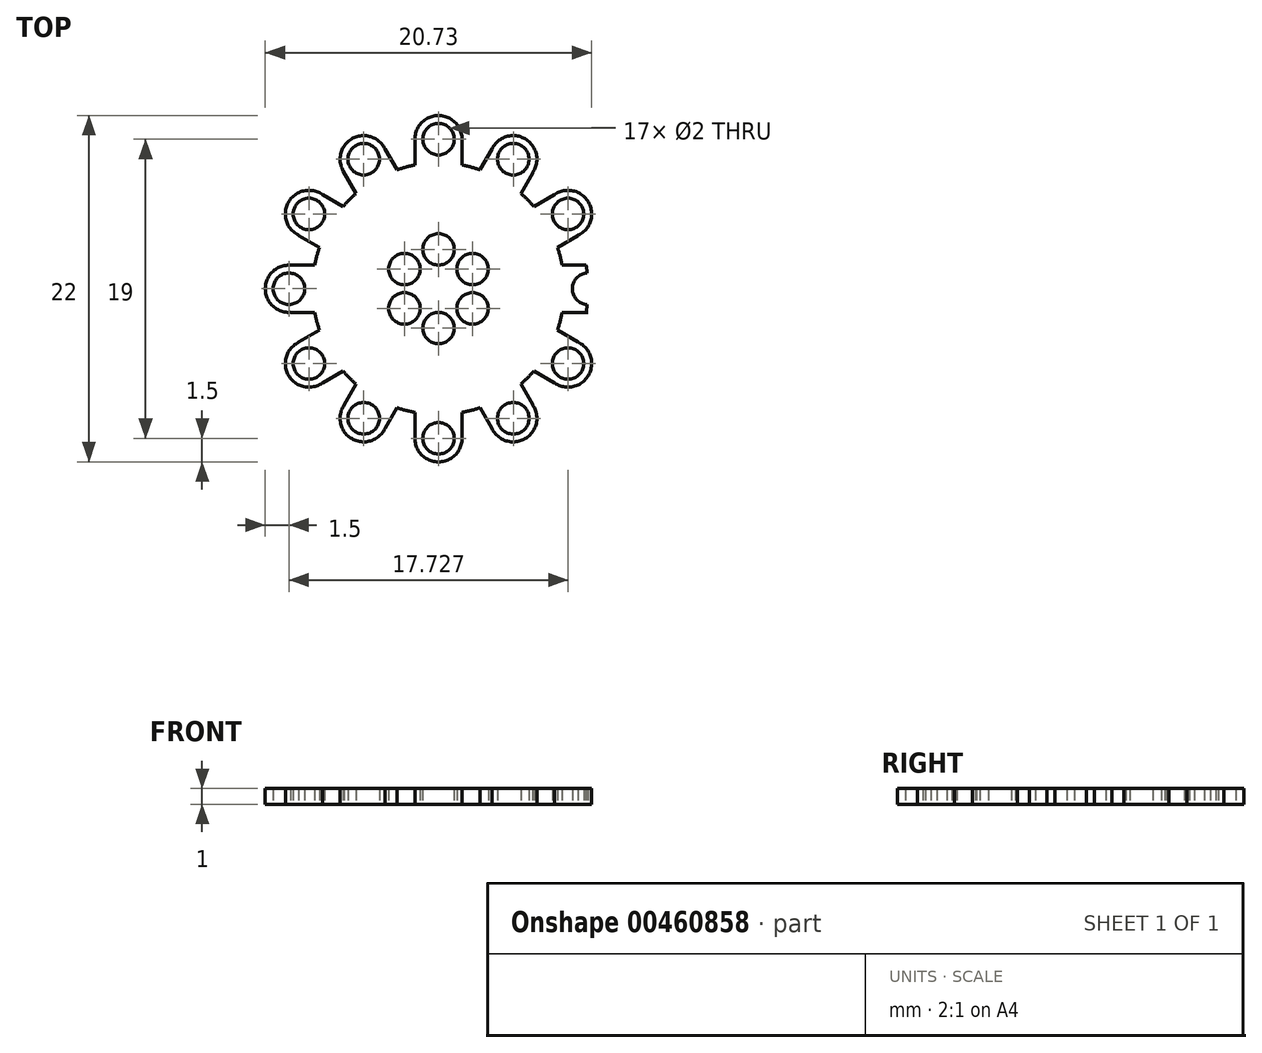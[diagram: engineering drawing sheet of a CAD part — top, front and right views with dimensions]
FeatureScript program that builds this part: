
annotation { "Feature Type Name" : "Feature", "Feature Type Description" : "" }
export const myFeature = defineFeature(function(context is Context, id is Id, definition is map)
    precondition{}
    {
        {
            var Q0;
            Q0=qCreatedBy(makeId("Top.planeOp"),FACE);
            var sketch = newSketch(context, id + "F0", { "sketchPlane" : qUnion([Q0])});
            skCircle(sketch, "E0", {"center": v(0, 0) * mm, "radius": 9.5 * mm});
            skCircle(sketch, "E1", {"center": v(0, 0) * mm, "radius": 2.5 * mm});
            skCircle(sketch, "E2", {"center": v(0, 2.5) * mm, "radius": 1 * mm});
            skCircle(sketch, "E3.1.0", {"center": v(-2.17, 1.25) * mm, "radius": 1 * mm});
            skCircle(sketch, "E3.2.0", {"center": v(-2.17, -1.25) * mm, "radius": 1 * mm});
            skCircle(sketch, "E3.3.0", {"center": v(0, -2.5) * mm, "radius": 1 * mm});
            skCircle(sketch, "E3.4.0", {"center": v(2.17, -1.25) * mm, "radius": 1 * mm});
            skCircle(sketch, "E3.5.0", {"center": v(2.17, 1.25) * mm, "radius": 1 * mm});
            skCircle(sketch, "E4", {"center": v(0, 0) * mm, "radius": 8 * mm});
            skLineSegment(sketch, "E5.anchor1", {"start": v(0, 0) * mm, "end": v(0, 8) * mm, "construction": true});
            skLineSegment(sketch, "E5.anchor2", {"start": v(0, 0) * mm, "end": v(-4, 6.93) * mm, "construction": true});
            skCircle(sketch, "E6", {"center": v(0, 9.5) * mm, "radius": 1 * mm});
            skCircle(sketch, "E7.1.0", {"center": v(-4.75, 8.23) * mm, "radius": 1 * mm});
            skCircle(sketch, "E7.2.0", {"center": v(-8.23, 4.75) * mm, "radius": 1 * mm});
            skCircle(sketch, "E7.3.0", {"center": v(-9.5, 0) * mm, "radius": 1 * mm});
            skCircle(sketch, "E7.4.0", {"center": v(-8.23, -4.75) * mm, "radius": 1 * mm});
            skCircle(sketch, "E7.5.0", {"center": v(-4.75, -8.23) * mm, "radius": 1 * mm});
            skCircle(sketch, "E7.6.0", {"center": v(0, -9.5) * mm, "radius": 1 * mm});
            skCircle(sketch, "E7.7.0", {"center": v(4.75, -8.23) * mm, "radius": 1 * mm});
            skCircle(sketch, "E7.8.0", {"center": v(8.23, -4.75) * mm, "radius": 1 * mm});
            skCircle(sketch, "E7.9.0", {"center": v(9.5, 0) * mm, "radius": 1 * mm});
            skCircle(sketch, "E7.10.0", {"center": v(8.23, 4.75) * mm, "radius": 1 * mm});
            skCircle(sketch, "E7.11.0", {"center": v(4.75, 8.23) * mm, "radius": 1 * mm});
            skArc(sketch, "E8", {"start": v(1.5, 9.38) * mm, "mid": v(0, 11) * mm, "end": v(-1.5, 9.38) * mm});
            skArc(sketch, "E9.1.0", {"start": v(-3.4, 8.87) * mm, "mid": v(-5.45, 9.55) * mm, "end": v(-6.05, 7.48) * mm});
            skArc(sketch, "E9.2.0", {"start": v(-7.38, 5.99) * mm, "mid": v(-9.53, 5.5) * mm, "end": v(-8.87, 3.4) * mm});
            skArc(sketch, "E9.3.0", {"start": v(-9.38, 1.5) * mm, "mid": v(-11, 0) * mm, "end": v(-9.38, -1.5) * mm});
            skArc(sketch, "E9.4.0", {"start": v(-8.87, -3.4) * mm, "mid": v(-9.53, -5.5) * mm, "end": v(-7.38, -5.99) * mm});
            skArc(sketch, "E9.5.0", {"start": v(-5.99, -7.38) * mm, "mid": v(-5.5, -9.53) * mm, "end": v(-3.4, -8.87) * mm});
            skArc(sketch, "E9.6.0", {"start": v(-1.5, -9.38) * mm, "mid": v(0, -11) * mm, "end": v(1.5, -9.38) * mm});
            skArc(sketch, "E9.7.0", {"start": v(3.4, -8.87) * mm, "mid": v(5.5, -9.53) * mm, "end": v(5.99, -7.38) * mm});
            skArc(sketch, "E9.8.0", {"start": v(7.38, -5.99) * mm, "mid": v(9.53, -5.5) * mm, "end": v(8.87, -3.4) * mm});
            skArc(sketch, "E9.9.0", {"start": v(9.38, -1.5) * mm, "mid": v(11, 0) * mm, "end": v(9.38, 1.5) * mm});
            skArc(sketch, "E9.10.0", {"start": v(8.87, 3.4) * mm, "mid": v(9.53, 5.5) * mm, "end": v(7.38, 5.99) * mm});
            skArc(sketch, "E9.11.0", {"start": v(5.99, 7.38) * mm, "mid": v(5.5, 9.53) * mm, "end": v(3.4, 8.87) * mm});
            skLineSegment(sketch, "E10", {"start": v(-1.5, 9.5) * mm, "end": v(-1.5, 7.86) * mm});
            skLineSegment(sketch, "E11", {"start": v(1.5, 9.5) * mm, "end": v(1.5, 7.86) * mm});
            skArc(sketch, "E12.1.0", {"start": v(-8.87, -3.4) * mm, "mid": v(-9.55, -5.45) * mm, "end": v(-7.48, -6.05) * mm});
            skLineSegment(sketch, "E13.1.0", {"start": v(-3.45, 8.98) * mm, "end": v(-2.63, 7.56) * mm});
            skLineSegment(sketch, "E13.2.0", {"start": v(-7.48, 6.05) * mm, "end": v(-6.06, 5.23) * mm});
            skLineSegment(sketch, "E13.3.0", {"start": v(-9.5, 1.5) * mm, "end": v(-7.86, 1.5) * mm});
            skLineSegment(sketch, "E13.4.0", {"start": v(-8.98, -3.45) * mm, "end": v(-7.56, -2.63) * mm});
            skLineSegment(sketch, "E13.5.0", {"start": v(-6.05, -7.48) * mm, "end": v(-5.23, -6.06) * mm});
            skLineSegment(sketch, "E13.6.0", {"start": v(-1.5, -9.5) * mm, "end": v(-1.5, -7.86) * mm});
            skLineSegment(sketch, "E13.7.0", {"start": v(3.45, -8.98) * mm, "end": v(2.63, -7.56) * mm});
            skLineSegment(sketch, "E13.8.0", {"start": v(7.48, -6.05) * mm, "end": v(6.06, -5.23) * mm});
            skLineSegment(sketch, "E13.9.0", {"start": v(9.5, -1.5) * mm, "end": v(7.86, -1.5) * mm});
            skLineSegment(sketch, "E13.10.0", {"start": v(8.98, 3.45) * mm, "end": v(7.56, 2.63) * mm});
            skLineSegment(sketch, "E13.11.0", {"start": v(6.05, 7.48) * mm, "end": v(5.23, 6.06) * mm});
            skLineSegment(sketch, "E14.1.0", {"start": v(-6.05, 7.48) * mm, "end": v(-5.23, 6.06) * mm});
            skLineSegment(sketch, "E14.2.0", {"start": v(-8.98, 3.45) * mm, "end": v(-7.56, 2.63) * mm});
            skLineSegment(sketch, "E14.3.0", {"start": v(-9.5, -1.5) * mm, "end": v(-7.86, -1.5) * mm});
            skLineSegment(sketch, "E14.4.0", {"start": v(-7.48, -6.05) * mm, "end": v(-6.06, -5.23) * mm});
            skLineSegment(sketch, "E14.5.0", {"start": v(-3.45, -8.98) * mm, "end": v(-2.63, -7.56) * mm});
            skLineSegment(sketch, "E14.6.0", {"start": v(1.5, -9.5) * mm, "end": v(1.5, -7.86) * mm});
            skLineSegment(sketch, "E14.7.0", {"start": v(6.05, -7.48) * mm, "end": v(5.23, -6.06) * mm});
            skLineSegment(sketch, "E14.8.0", {"start": v(8.98, -3.45) * mm, "end": v(7.56, -2.63) * mm});
            skLineSegment(sketch, "E14.9.0", {"start": v(9.5, 1.5) * mm, "end": v(7.86, 1.5) * mm});
            skLineSegment(sketch, "E14.10.0", {"start": v(7.48, 6.05) * mm, "end": v(6.06, 5.23) * mm});
            skLineSegment(sketch, "E14.11.0", {"start": v(3.45, 8.98) * mm, "end": v(2.63, 7.56) * mm});
            skSolve(sketch);
        }
        {
            var Q0;
            {var subQ11=sQuery(id+"F0.wireOp",EDGE,"E3.5.0");var subQ12=sQuery(id+"F0.wireOp",EDGE,"E1");var subQ13=makeQuery(id+"F0.imprint","INTERSECT",VERTEX,{"disambiguationData":[OD(0.0)],"derivedFrom":[subQ12,subQ11]});Q0=makeQuery(id+"F0.imprint","IMPRINT",FACE,{"disambiguationData":[TD([[makeQuery(id+"F0.imprint","IMPRINT",EDGE,{"disambiguationData":[TD([[subQ13,-1.0]])],"derivedFrom":subQ12}),-1.0]])]});}
            var Q1;
            {var subQ0=sQuery(id+"F0.wireOp",EDGE,"E9.8.0");var subQ1=sQuery(id+"F0.wireOp",EDGE,"E0");var subQ12=makeQuery(id+"F0.imprint","INTERSECT",VERTEX,{"disambiguationData":[OD(0.0)],"derivedFrom":[subQ1,subQ0]});Q1=makeQuery(id+"F0.imprint","IMPRINT",FACE,{"disambiguationData":[TD([[makeQuery(id+"F0.imprint","IMPRINT",EDGE,{"disambiguationData":[TD([[subQ12,1.0]])],"derivedFrom":subQ1}),1.0]])]});}
            var Q2;
            {var subQ0=sQuery(id+"F0.wireOp",EDGE,"E9.8.0");var subQ1=sQuery(id+"F0.wireOp",EDGE,"E0");var subQ2=makeQuery(id+"F0.imprint","INTERSECT",VERTEX,{"disambiguationData":[OD(0.0)],"derivedFrom":[subQ1,subQ0]});Q2=makeQuery(id+"F0.imprint","IMPRINT",FACE,{"disambiguationData":[TD([[makeQuery(id+"F0.imprint","IMPRINT",EDGE,{"disambiguationData":[TD([[subQ2,-1.0]])],"derivedFrom":subQ1}),-1.0]])]});}
            var Q3;
            {var subQ0=sQuery(id+"F0.wireOp",EDGE,"E9.9.0");var subQ1=sQuery(id+"F0.wireOp",EDGE,"E0");var subQ7=makeQuery(id+"F0.imprint","INTERSECT",VERTEX,{"disambiguationData":[OD(1.0)],"derivedFrom":[subQ1,subQ0]});Q3=makeQuery(id+"F0.imprint","IMPRINT",FACE,{"disambiguationData":[TD([[makeQuery(id+"F0.imprint","IMPRINT",EDGE,{"disambiguationData":[TD([[subQ7,1.0]])],"derivedFrom":subQ1}),1.0]])]});}
            var Q4;
            {var subQ0=sQuery(id+"F0.wireOp",EDGE,"E9.9.0");var subQ1=sQuery(id+"F0.wireOp",EDGE,"E0");var subQ7=makeQuery(id+"F0.imprint","INTERSECT",VERTEX,{"disambiguationData":[OD(1.0)],"derivedFrom":[subQ1,subQ0]});Q4=makeQuery(id+"F0.imprint","IMPRINT",FACE,{"disambiguationData":[TD([[makeQuery(id+"F0.imprint","IMPRINT",EDGE,{"disambiguationData":[TD([[subQ7,1.0]])],"derivedFrom":subQ1}),-1.0]])]});}
            var Q5;
            {var subQ0=sQuery(id+"F0.wireOp",EDGE,"E9.10.0");var subQ1=sQuery(id+"F0.wireOp",EDGE,"E0");var subQ8=makeQuery(id+"F0.imprint","INTERSECT",VERTEX,{"disambiguationData":[OD(0.0)],"derivedFrom":[subQ1,subQ0]});Q5=makeQuery(id+"F0.imprint","IMPRINT",FACE,{"disambiguationData":[TD([[makeQuery(id+"F0.imprint","IMPRINT",EDGE,{"disambiguationData":[TD([[subQ8,1.0]])],"derivedFrom":subQ1}),1.0]])]});}
            var Q6;
            {var subQ1=sQuery(id+"F0.wireOp",EDGE,"E0");var subQ4=sQuery(id+"F0.wireOp",EDGE,"E9.10.0");var subQ5=makeQuery(id+"F0.imprint","INTERSECT",VERTEX,{"disambiguationData":[OD(0.0)],"derivedFrom":[subQ1,subQ4]});Q6=makeQuery(id+"F0.imprint","IMPRINT",FACE,{"disambiguationData":[TD([[makeQuery(id+"F0.imprint","IMPRINT",EDGE,{"disambiguationData":[TD([[subQ5,-1.0]])],"derivedFrom":subQ1}),-1.0]])]});}
            var Q7;
            {var subQ0=sQuery(id+"F0.wireOp",EDGE,"E9.11.0");var subQ1=sQuery(id+"F0.wireOp",EDGE,"E0");var subQ7=makeQuery(id+"F0.imprint","INTERSECT",VERTEX,{"disambiguationData":[OD(0.0)],"derivedFrom":[subQ1,subQ0]});Q7=makeQuery(id+"F0.imprint","IMPRINT",FACE,{"disambiguationData":[TD([[makeQuery(id+"F0.imprint","IMPRINT",EDGE,{"disambiguationData":[TD([[subQ7,1.0]])],"derivedFrom":subQ1}),1.0]])]});}
            var Q8;
            {var subQ0=sQuery(id+"F0.wireOp",EDGE,"E9.11.0");var subQ1=sQuery(id+"F0.wireOp",EDGE,"E0");var subQ2=makeQuery(id+"F0.imprint","INTERSECT",VERTEX,{"disambiguationData":[OD(0.0)],"derivedFrom":[subQ1,subQ0]});Q8=makeQuery(id+"F0.imprint","IMPRINT",FACE,{"disambiguationData":[TD([[makeQuery(id+"F0.imprint","IMPRINT",EDGE,{"disambiguationData":[TD([[subQ2,-1.0]])],"derivedFrom":subQ1}),-1.0]])]});}
            var Q9;
            {var subQ0=sQuery(id+"F0.wireOp",EDGE,"E8");var subQ1=sQuery(id+"F0.wireOp",EDGE,"E0");var subQ9=makeQuery(id+"F0.imprint","INTERSECT",VERTEX,{"disambiguationData":[OD(0.0)],"derivedFrom":[subQ1,subQ0]});Q9=makeQuery(id+"F0.imprint","IMPRINT",FACE,{"disambiguationData":[TD([[makeQuery(id+"F0.imprint","IMPRINT",EDGE,{"disambiguationData":[TD([[subQ9,1.0]])],"derivedFrom":subQ1}),1.0]])]});}
            var Q10;
            {var subQ1=sQuery(id+"F0.wireOp",EDGE,"E0");var subQ4=sQuery(id+"F0.wireOp",EDGE,"E8");var subQ5=makeQuery(id+"F0.imprint","INTERSECT",VERTEX,{"disambiguationData":[OD(0.0)],"derivedFrom":[subQ1,subQ4]});Q10=makeQuery(id+"F0.imprint","IMPRINT",FACE,{"disambiguationData":[TD([[makeQuery(id+"F0.imprint","IMPRINT",EDGE,{"disambiguationData":[TD([[subQ5,-1.0]])],"derivedFrom":subQ1}),-1.0]])]});}
            var Q11;
            {var subQ1=sQuery(id+"F0.wireOp",EDGE,"E0");var subQ9=makeQuery(id+"F0.imprint","INTERSECT",VERTEX,{"derivedFrom":[subQ1,sQuery(id+"F0.wireOp",EDGE,"E9.1.0")]});Q11=makeQuery(id+"F0.imprint","IMPRINT",FACE,{"disambiguationData":[TD([[makeQuery(id+"F0.imprint","IMPRINT",EDGE,{"disambiguationData":[TD([[subQ9,1.0]])],"derivedFrom":subQ1}),1.0]])]});}
            var Q12;
            {var subQ0=sQuery(id+"F0.wireOp",EDGE,"E9.1.0");var subQ1=sQuery(id+"F0.wireOp",EDGE,"E0");var subQ2=makeQuery(id+"F0.imprint","INTERSECT",VERTEX,{"derivedFrom":[subQ1,subQ0]});Q12=makeQuery(id+"F0.imprint","IMPRINT",FACE,{"disambiguationData":[TD([[makeQuery(id+"F0.imprint","IMPRINT",EDGE,{"disambiguationData":[TD([[subQ2,-1.0]])],"derivedFrom":subQ1}),-1.0]])]});}
            var Q13;
            {var subQ0=sQuery(id+"F0.wireOp",EDGE,"E9.2.0");var subQ1=sQuery(id+"F0.wireOp",EDGE,"E0");var subQ7=makeQuery(id+"F0.imprint","INTERSECT",VERTEX,{"disambiguationData":[OD(0.0)],"derivedFrom":[subQ1,subQ0]});Q13=makeQuery(id+"F0.imprint","IMPRINT",FACE,{"disambiguationData":[TD([[makeQuery(id+"F0.imprint","IMPRINT",EDGE,{"disambiguationData":[TD([[subQ7,1.0]])],"derivedFrom":subQ1}),1.0]])]});}
            var Q14;
            {var subQ0=sQuery(id+"F0.wireOp",EDGE,"E9.2.0");var subQ1=sQuery(id+"F0.wireOp",EDGE,"E0");var subQ2=makeQuery(id+"F0.imprint","INTERSECT",VERTEX,{"disambiguationData":[OD(0.0)],"derivedFrom":[subQ1,subQ0]});Q14=makeQuery(id+"F0.imprint","IMPRINT",FACE,{"disambiguationData":[TD([[makeQuery(id+"F0.imprint","IMPRINT",EDGE,{"disambiguationData":[TD([[subQ2,-1.0]])],"derivedFrom":subQ1}),-1.0]])]});}
            var Q15;
            {var subQ0=sQuery(id+"F0.wireOp",EDGE,"E9.3.0");var subQ1=sQuery(id+"F0.wireOp",EDGE,"E0");var subQ7=makeQuery(id+"F0.imprint","INTERSECT",VERTEX,{"disambiguationData":[OD(0.0)],"derivedFrom":[subQ1,subQ0]});Q15=makeQuery(id+"F0.imprint","IMPRINT",FACE,{"disambiguationData":[TD([[makeQuery(id+"F0.imprint","IMPRINT",EDGE,{"disambiguationData":[TD([[subQ7,1.0]])],"derivedFrom":subQ1}),1.0]])]});}
            var Q16;
            {var subQ0=sQuery(id+"F0.wireOp",EDGE,"E9.3.0");var subQ1=sQuery(id+"F0.wireOp",EDGE,"E0");var subQ2=makeQuery(id+"F0.imprint","INTERSECT",VERTEX,{"disambiguationData":[OD(0.0)],"derivedFrom":[subQ1,subQ0]});Q16=makeQuery(id+"F0.imprint","IMPRINT",FACE,{"disambiguationData":[TD([[makeQuery(id+"F0.imprint","IMPRINT",EDGE,{"disambiguationData":[TD([[subQ2,-1.0]])],"derivedFrom":subQ1}),-1.0]])]});}
            var Q17;
            {var subQ0=sQuery(id+"F0.wireOp",EDGE,"E9.4.0");var subQ1=sQuery(id+"F0.wireOp",EDGE,"E0");var subQ11=makeQuery(id+"F0.imprint","INTERSECT",VERTEX,{"disambiguationData":[OD(0.0)],"derivedFrom":[subQ1,subQ0]});Q17=makeQuery(id+"F0.imprint","IMPRINT",FACE,{"disambiguationData":[TD([[makeQuery(id+"F0.imprint","IMPRINT",EDGE,{"disambiguationData":[TD([[subQ11,1.0]])],"derivedFrom":subQ1}),1.0]])]});}
            var Q18;
            {var subQ1=sQuery(id+"F0.wireOp",EDGE,"E0");var subQ4=sQuery(id+"F0.wireOp",EDGE,"E9.4.0");var subQ5=makeQuery(id+"F0.imprint","INTERSECT",VERTEX,{"disambiguationData":[OD(0.0)],"derivedFrom":[subQ1,subQ4]});Q18=makeQuery(id+"F0.imprint","IMPRINT",FACE,{"disambiguationData":[TD([[makeQuery(id+"F0.imprint","IMPRINT",EDGE,{"disambiguationData":[TD([[subQ5,-1.0]])],"derivedFrom":subQ1}),-1.0]])]});}
            var Q19;
            {var subQ0=sQuery(id+"F0.wireOp",EDGE,"E9.5.0");var subQ1=sQuery(id+"F0.wireOp",EDGE,"E0");var subQ12=makeQuery(id+"F0.imprint","INTERSECT",VERTEX,{"disambiguationData":[OD(0.0)],"derivedFrom":[subQ1,subQ0]});Q19=makeQuery(id+"F0.imprint","IMPRINT",FACE,{"disambiguationData":[TD([[makeQuery(id+"F0.imprint","IMPRINT",EDGE,{"disambiguationData":[TD([[subQ12,1.0]])],"derivedFrom":subQ1}),1.0]])]});}
            var Q20;
            {var subQ0=sQuery(id+"F0.wireOp",EDGE,"E9.5.0");var subQ1=sQuery(id+"F0.wireOp",EDGE,"E0");var subQ2=makeQuery(id+"F0.imprint","INTERSECT",VERTEX,{"disambiguationData":[OD(0.0)],"derivedFrom":[subQ1,subQ0]});Q20=makeQuery(id+"F0.imprint","IMPRINT",FACE,{"disambiguationData":[TD([[makeQuery(id+"F0.imprint","IMPRINT",EDGE,{"disambiguationData":[TD([[subQ2,-1.0]])],"derivedFrom":subQ1}),-1.0]])]});}
            var Q21;
            {var subQ0=sQuery(id+"F0.wireOp",EDGE,"E9.6.0");var subQ1=sQuery(id+"F0.wireOp",EDGE,"E0");var subQ8=makeQuery(id+"F0.imprint","INTERSECT",VERTEX,{"disambiguationData":[OD(0.0)],"derivedFrom":[subQ1,subQ0]});Q21=makeQuery(id+"F0.imprint","IMPRINT",FACE,{"disambiguationData":[TD([[makeQuery(id+"F0.imprint","IMPRINT",EDGE,{"disambiguationData":[TD([[subQ8,1.0]])],"derivedFrom":subQ1}),1.0]])]});}
            var Q22;
            {var subQ0=sQuery(id+"F0.wireOp",EDGE,"E9.7.0");var subQ1=sQuery(id+"F0.wireOp",EDGE,"E0");var subQ11=makeQuery(id+"F0.imprint","INTERSECT",VERTEX,{"disambiguationData":[OD(0.0)],"derivedFrom":[subQ1,subQ0]});Q22=makeQuery(id+"F0.imprint","IMPRINT",FACE,{"disambiguationData":[TD([[makeQuery(id+"F0.imprint","IMPRINT",EDGE,{"disambiguationData":[TD([[subQ11,1.0]])],"derivedFrom":subQ1}),1.0]])]});}
            var Q23;
            {var subQ0=sQuery(id+"F0.wireOp",EDGE,"E9.7.0");var subQ1=sQuery(id+"F0.wireOp",EDGE,"E0");var subQ2=makeQuery(id+"F0.imprint","INTERSECT",VERTEX,{"disambiguationData":[OD(0.0)],"derivedFrom":[subQ1,subQ0]});Q23=makeQuery(id+"F0.imprint","IMPRINT",FACE,{"disambiguationData":[TD([[makeQuery(id+"F0.imprint","IMPRINT",EDGE,{"disambiguationData":[TD([[subQ2,-1.0]])],"derivedFrom":subQ1}),-1.0]])]});}
            var Q24;
            {var subQ0=sQuery(id+"F0.wireOp",EDGE,"E9.6.0");var subQ1=sQuery(id+"F0.wireOp",EDGE,"E0");var subQ2=makeQuery(id+"F0.imprint","INTERSECT",VERTEX,{"disambiguationData":[OD(0.0)],"derivedFrom":[subQ1,subQ0]});Q24=makeQuery(id+"F0.imprint","IMPRINT",FACE,{"disambiguationData":[TD([[makeQuery(id+"F0.imprint","IMPRINT",EDGE,{"disambiguationData":[TD([[subQ2,-1.0]])],"derivedFrom":subQ1}),-1.0]])]});}
            var Q25;
            {var subQ0=sQuery(id+"F0.wireOp",EDGE,"E3.5.0");var subQ1=sQuery(id+"F0.wireOp",EDGE,"E1");var subQ11=makeQuery(id+"F0.imprint","INTERSECT",VERTEX,{"disambiguationData":[OD(0.0)],"derivedFrom":[subQ1,subQ0]});Q25=makeQuery(id+"F0.imprint","IMPRINT",FACE,{"disambiguationData":[TD([[makeQuery(id+"F0.imprint","IMPRINT",EDGE,{"disambiguationData":[TD([[subQ11,-1.0]])],"derivedFrom":subQ1}),1.0]])]});}
            extrude(context, id + "F1", {"entities" : qUnion([Q0, Q1, Q2, Q3, Q4, Q5, Q6, Q7, Q8, Q9, Q10, Q11, Q12, Q13, Q14, Q15, Q16, Q17, Q18, Q19, Q20, Q21, Q22, Q23, Q24, Q25]), "depth" : 1 * mm});
        }
    });
